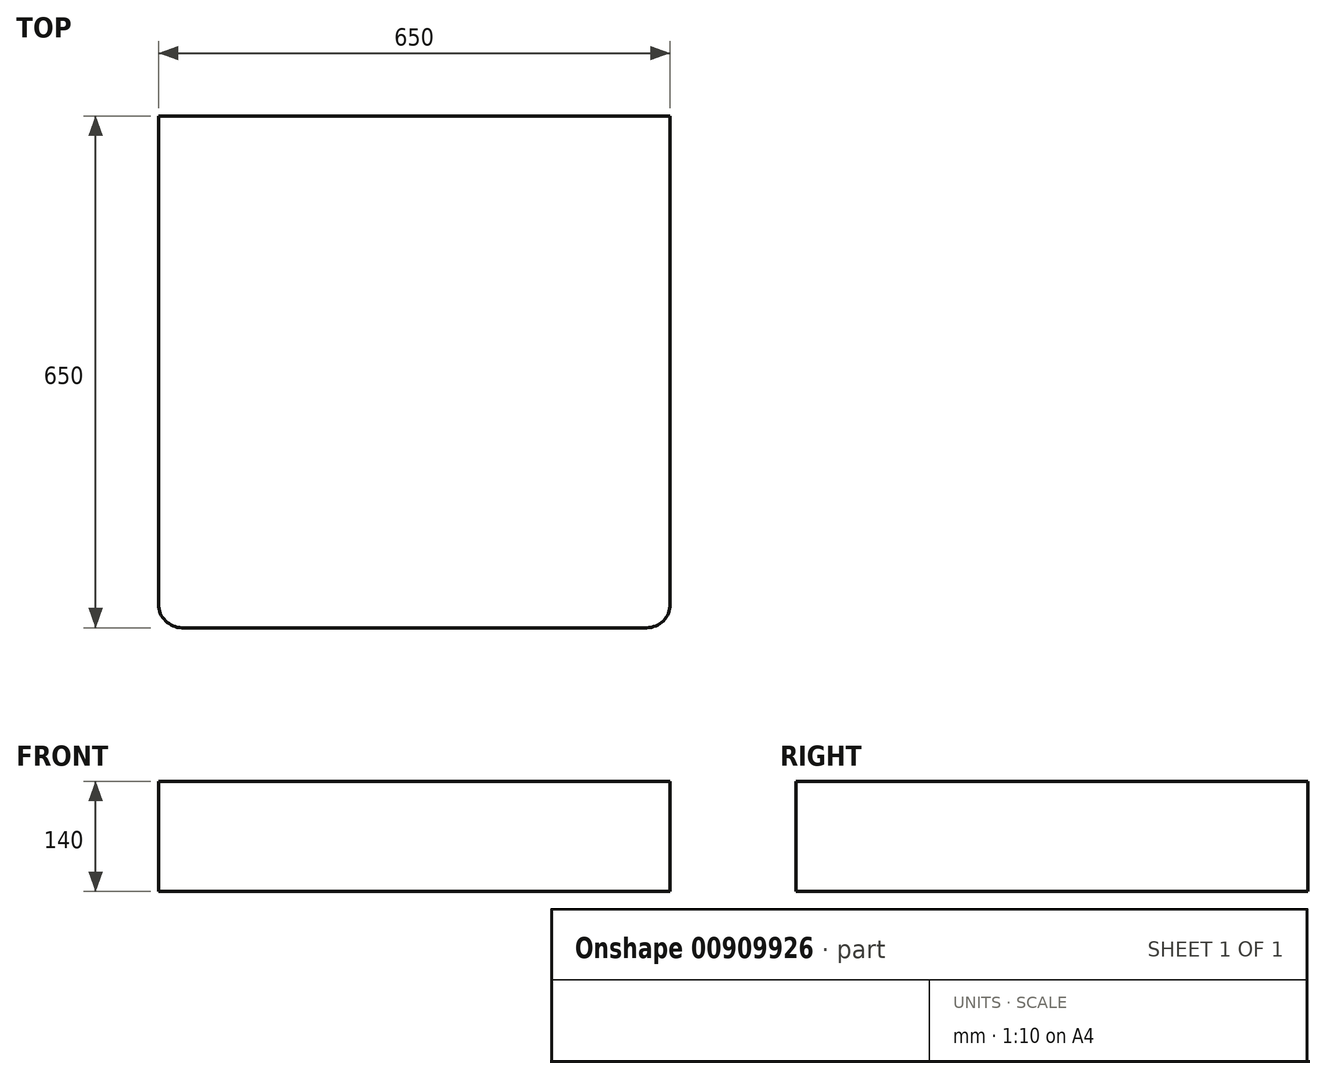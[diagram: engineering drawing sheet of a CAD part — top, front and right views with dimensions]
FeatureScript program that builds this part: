
annotation { "Feature Type Name" : "Feature", "Feature Type Description" : "" }
export const myFeature = defineFeature(function(context is Context, id is Id, definition is map)
    precondition{}
    {
        {
            var Q0;
            Q0=qCreatedBy(makeId("Top.planeOp"),FACE);
            var sketch = newSketch(context, id + "F0", { "sketchPlane" : qUnion([Q0])});
            skLineSegment(sketch, "E0.bottom", {"start": v(0, 0) * mm, "end": v(650, 0) * mm});
            skLineSegment(sketch, "E0.top", {"start": v(30, -650) * mm, "end": v(620, -650) * mm});
            skLineSegment(sketch, "E0.left", {"start": v(0, 0) * mm, "end": v(0, -620) * mm});
            skLineSegment(sketch, "E0.right", {"start": v(650, 0) * mm, "end": v(650, -620) * mm});
            skPoint(sketch, "E1.visualSharp", {"position": v(0, -650) * mm});
            skArc(sketch, "E1.filletArc", {"start": v(0, -620) * mm, "mid": v(8.79, -641.21) * mm, "end": v(30, -650) * mm});
            skPoint(sketch, "E2.visualSharp", {"position": v(650, -650) * mm});
            skArc(sketch, "E2.filletArc", {"start": v(620, -650) * mm, "mid": v(641.21, -641.21) * mm, "end": v(650, -620) * mm});
            skSolve(sketch);
        }
        {
            var Q0;
            Q0=makeQuery(id+"F0.imprint","IMPRINT",FACE,{"disambiguationData":[TD([[makeQuery(id+"F0.imprint","IMPRINT",EDGE,{"derivedFrom":sQuery(id+"F0.wireOp",EDGE,"E0.bottom")}),-1.0]])]});
            extrude(context, id + "F1", {"entities" : qUnion([Q0]), "depth" : 140 * mm, "offsetDistance" : 25 * mm});
        }
    });
